# Revit family: FU_Chair_Sandler_SOFIA 2-3
name_source: partatom
category: Furniture
units: mm (PartAtom-declared; Revit-internal decimal feet)

## family parameters
Always vertical = Yes
Cut with Voids When Loaded = No
OmniClass Number = 23.40.20.00
OmniClass Title = General Furniture and Specialties
Room Calculation Point = No
Shared = No
Work Plane-Based = No

## types (1)
- Sofia 2.3
    Default Elevation = 0 mm  [stored 0 ft]
    Depth = 680 mm  [stored 2.23097 ft]
    Description = Armchair, seat frame with rounded edges. Shell with two foam elements. Webbed seat. Upholstered onto the frame. 4-spoke swivel Nylon base.
    Frame = Nylon - Black
    Height = 910 mm
    Manufacturer = Sandler
    Model = Sofia 2.3
    Seat = Fabric - Gravity - Wheat CPC21
    URL = https://www.sandlerseating.com
    Width = 630 mm  [stored 2.06693 ft]

note: [stored X ft] marks values corroborated as IEEE doubles in the binary element streams (Revit-internal decimal feet)

## geometry (parser evidence)
native form markers: Sweep x9
no freeform markers — native parametric forms only
